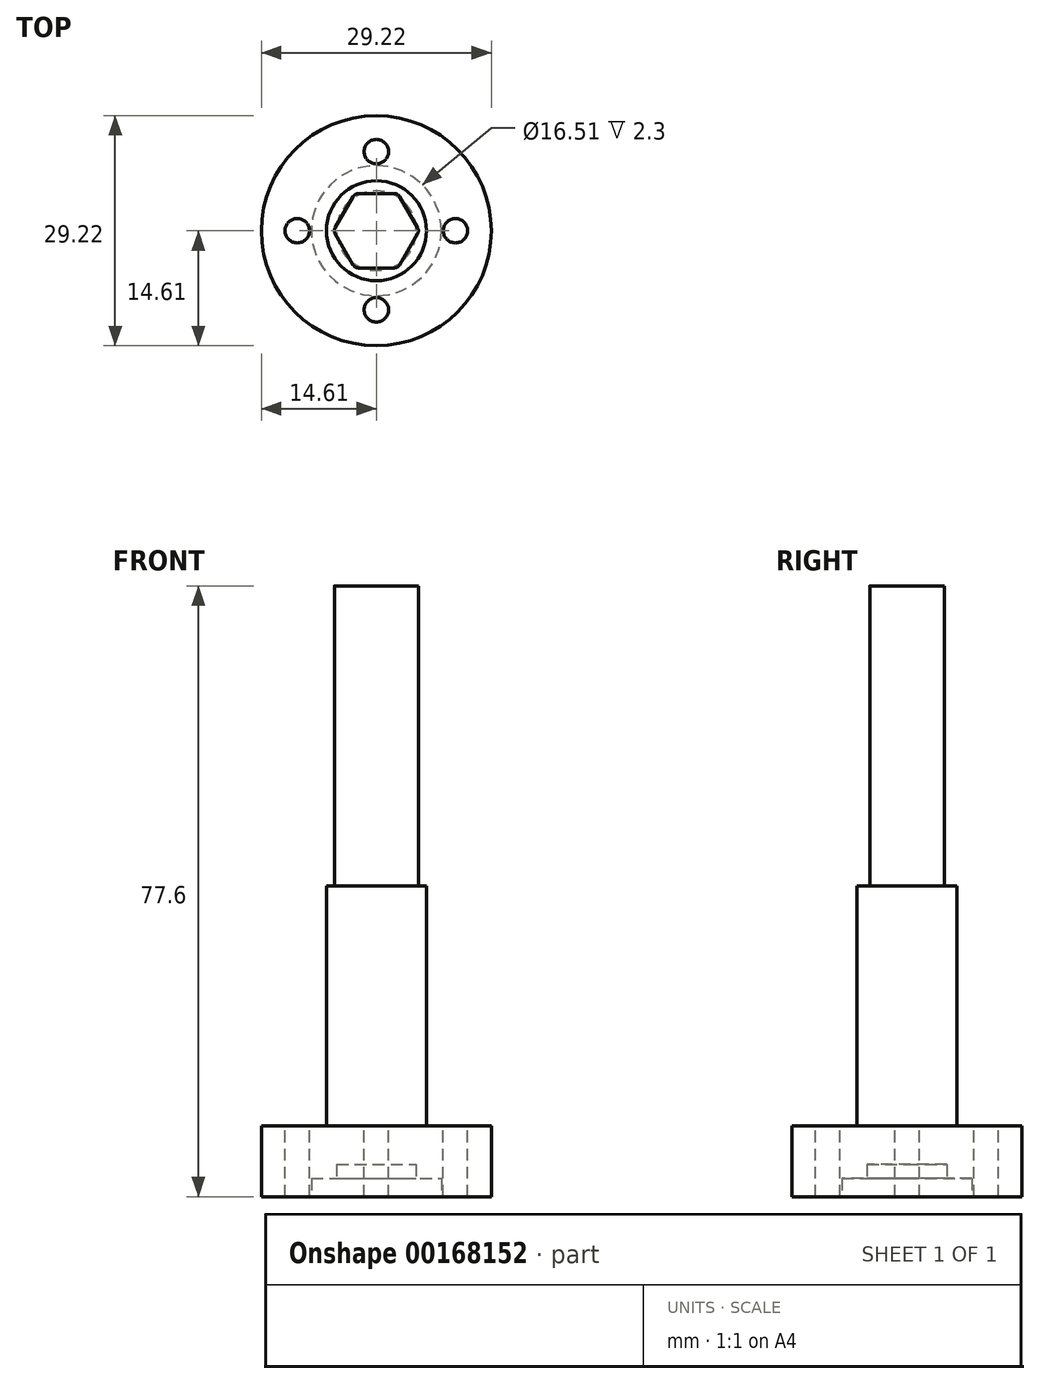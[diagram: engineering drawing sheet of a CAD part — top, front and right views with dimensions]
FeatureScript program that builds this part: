
annotation { "Feature Type Name" : "Feature", "Feature Type Description" : "" }
export const myFeature = defineFeature(function(context is Context, id is Id, definition is map)
    precondition{}
    {
        {
            var Q0;
            Q0=qCreatedBy(makeId("Top.planeOp"),FACE);
            var sketch = newSketch(context, id + "F0", { "sketchPlane" : qUnion([Q0])});
            skCircle(sketch, "E0", {"center": v(0, 0) * mm, "radius": 14.6 * mm});
            skSolve(sketch);
        }
        {
            var Q0;
            Q0=makeQuery(id+"F0.imprint","IMPRINT",FACE,{"disambiguationData":[TD([[makeQuery(id+"F0.imprint","IMPRINT",EDGE,{"derivedFrom":sQuery(id+"F0.wireOp",EDGE,"E0")}),1.0]])]});
            extrude(context, id + "F1", {"entities" : qUnion([Q0]), "depth" : 9.02 * mm});
        }
        {
            var Q0;
            Q0=makeQuery(id+"F1.opExtrude","CAP_FACE",FACE,{"disambiguationData":[OSD([sQuery(id+"F0.wireOp",EDGE,"E0")])],"isStart":false});
            var sketch = newSketch(context, id + "F2", { "sketchPlane" : qUnion([Q0])});
            skCircle(sketch, "E1", {"center": v(0, 0) * mm, "radius": 6.35 * mm});
            skSolve(sketch);
        }
        {
            var Q0;
            Q0=qSketchRegion(id+"F2",true);
            extrude(context, id + "F3", {"entities" : qUnion([Q0]), "operationType" : NewBodyOperationType.ADD, "depth" : 30.48 * mm});
        }
        {
            var Q0;
            Q0=makeQuery(id+"F3.opExtrude","CAP_FACE",FACE,{"disambiguationData":[OSD([sQuery(id+"F2.wireOp",EDGE,"E1")])],"isStart":false});
            var sketch = newSketch(context, id + "F4", { "sketchPlane" : qUnion([Q0])});
            skCircle(sketch, "E2.cCircle", {"center": v(0, 0) * mm, "radius": 4.72 * mm, "construction": true});
            skLineSegment(sketch, "E2.0", {"start": v(5.46, 0) * mm, "end": v(2.73, -4.72) * mm});
            skLineSegment(sketch, "E2.1", {"start": v(2.73, -4.72) * mm, "end": v(-2.73, -4.72) * mm});
            skLineSegment(sketch, "E2.2", {"start": v(-2.73, -4.72) * mm, "end": v(-5.46, 0) * mm});
            skLineSegment(sketch, "E2.3", {"start": v(-5.46, 0) * mm, "end": v(-2.73, 4.72) * mm});
            skLineSegment(sketch, "E2.4", {"start": v(-2.73, 4.72) * mm, "end": v(2.73, 4.72) * mm});
            skLineSegment(sketch, "E2.5", {"start": v(2.73, 4.72) * mm, "end": v(5.46, 0) * mm});
            skPoint(sketch, "E2.0.midPoint", {"position": v(4.1, -2.36) * mm});
            skSolve(sketch);
        }
        {
            var Q0;
            Q0=makeQuery(id+"F4.imprint","IMPRINT",FACE,{"disambiguationData":[TD([[makeQuery(id+"F4.imprint","IMPRINT",EDGE,{"derivedFrom":sQuery(id+"F4.wireOp",EDGE,"E2.0")}),-1.0]])]});
            extrude(context, id + "F5", {"entities" : qUnion([Q0]), "operationType" : NewBodyOperationType.ADD, "depth" : 38.1 * mm});
        }
        {
            var Q0;
            Q0=makeQuery(id+"F1.opExtrude","CAP_FACE",FACE,{"disambiguationData":[OSD([sQuery(id+"F0.wireOp",EDGE,"E0")])],"isStart":true});
            var sketch = newSketch(context, id + "F6", { "sketchPlane" : qUnion([Q0])});
            skCircle(sketch, "E3", {"center": v(0, 0) * mm, "radius": 8.26 * mm});
            skSolve(sketch);
        }
        {
            var Q0;
            Q0=qSketchRegion(id+"F6",true);
            extrude(context, id + "F7", {"entities" : qUnion([Q0]), "operationType" : NewBodyOperationType.REMOVE, "oppositeDirection" : true, "depth" : 2.3 * mm});
        }
        {
            var Q0;
            Q0=makeQuery(id+"F1.opExtrude","CAP_FACE",FACE,{"disambiguationData":[OSD([sQuery(id+"F0.wireOp",EDGE,"E0")])],"isStart":true});
            var sketch = newSketch(context, id + "F8", { "sketchPlane" : qUnion([Q0])});
            skCircle(sketch, "E4", {"center": v(0, 0) * mm, "radius": 5.06 * mm});
            skSolve(sketch);
        }
        {
            var Q0;
            Q0=qSketchRegion(id+"F8",true);
            extrude(context, id + "F9", {"entities" : qUnion([Q0]), "operationType" : NewBodyOperationType.REMOVE, "oppositeDirection" : true, "depth" : 4.1 * mm});
        }
        {
            var Q0;
            Q0=makeQuery(id+"F1.opExtrude","CAP_FACE",FACE,{"disambiguationData":[OSD([sQuery(id+"F0.wireOp",EDGE,"E0")])],"isStart":false});
            var sketch = newSketch(context, id + "F10", { "sketchPlane" : qUnion([Q0])});
            skPoint(sketch, "E5", {"position": v(-10.05, 0) * mm});
            skPoint(sketch, "E6", {"position": v(0, 10.05) * mm});
            skPoint(sketch, "E7", {"position": v(10.05, 0) * mm});
            skPoint(sketch, "E8", {"position": v(0, -10.05) * mm});
            skCircle(sketch, "E9", {"center": v(0, 0) * mm, "radius": 10.05 * mm, "construction": true});
            skSolve(sketch);
        }
        {
            var Q0;
            Q0=sQuery(id+"F10.wireOp",VERTEX,"E8");
            var Q1;
            Q1=sQuery(id+"F10.wireOp",VERTEX,"E5");
            var Q2;
            Q2=sQuery(id+"F10.wireOp",VERTEX,"E6");
            var Q3;
            Q3=sQuery(id+"F10.wireOp",VERTEX,"E7");
            var Q4;
            Q4=makeQuery(id+"F1.opExtrude","SWEPT_BODY",BODY,{"disambiguationData":[OSD([sQuery(id+"F0.wireOp",EDGE,"E0")])]});
            hole(context, id + "F11", {"style" : HoleStyle.SIMPLE, "endStyle" : HoleEndStyle.THROUGH, "holeDiameter" : 3.1 * mm, "locations" : qUnion([Q0, Q1, Q2, Q3]), "scope" : qUnion([Q4]), "isTappedThrough" : true});
        }
        {
            var Q0;
            Q0=makeQuery(id+"F5.opExtrude","SWEPT_EDGE",EDGE,{"disambiguationData":[OSD([sQuery(id+"F4.wireOp",EDGE,"E2.1"),sQuery(id+"F4.wireOp",EDGE,"E2.2")])]});
            var Q1;
            Q1=makeQuery(id+"F5.opExtrude","SWEPT_EDGE",EDGE,{"disambiguationData":[OSD([sQuery(id+"F4.wireOp",EDGE,"E2.0"),sQuery(id+"F4.wireOp",EDGE,"E2.1")])]});
            var Q2;
            Q2=makeQuery(id+"F5.opExtrude","SWEPT_EDGE",EDGE,{"disambiguationData":[OSD([sQuery(id+"F4.wireOp",EDGE,"E2.0"),sQuery(id+"F4.wireOp",EDGE,"E2.5")])]});
            var Q3;
            Q3=makeQuery(id+"F5.opExtrude","SWEPT_EDGE",EDGE,{"disambiguationData":[OSD([sQuery(id+"F4.wireOp",EDGE,"E2.4"),sQuery(id+"F4.wireOp",EDGE,"E2.5")])]});
            var Q4;
            Q4=makeQuery(id+"F5.opExtrude","SWEPT_EDGE",EDGE,{"disambiguationData":[OSD([sQuery(id+"F4.wireOp",EDGE,"E2.3"),sQuery(id+"F4.wireOp",EDGE,"E2.4")])]});
            var Q5;
            Q5=makeQuery(id+"F5.opExtrude","SWEPT_EDGE",EDGE,{"disambiguationData":[OSD([sQuery(id+"F4.wireOp",EDGE,"E2.2"),sQuery(id+"F4.wireOp",EDGE,"E2.3")])]});
            fillet(context, id + "F12", {"entities" : qUnion([Q0, Q1, Q2, Q3, Q4, Q5]), "radius" : 0.76 * mm, "tangentPropagation" : true, "allowEdgeOverflow" : false});
        }
    });
